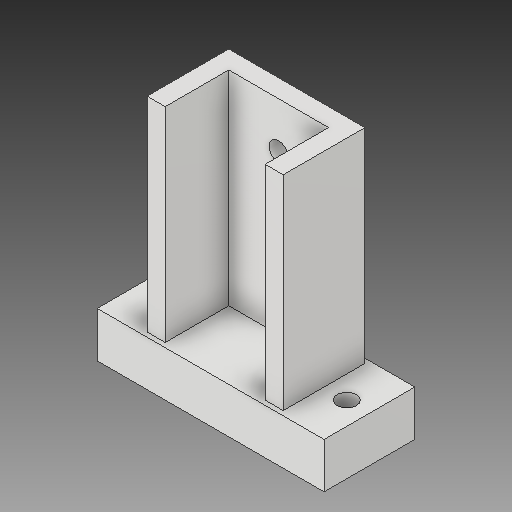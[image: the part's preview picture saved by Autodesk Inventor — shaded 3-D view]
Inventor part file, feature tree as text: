
AUTODESK INVENTOR PART (.ipt)
format: ipt  version: 2019 (Build 230136000, 136)  size: 143,872 bytes
history: native  units: mm
features: extrude x4, sketch x4, projected_geometry x1
ambient origin geometry x8: Origin, YZ Plane, XZ Plane, XY Plane, X Axis, Y Axis, Z Axis, Center Point
bodies: Body1 (feature_tree)
feature tree (9):
  extrude  "Extrusion3"  Depth=50.0mm
  extrude  "Extrusion4"  Depth=22.0mm
  extrude  "Extrusion5"  Depth=4.0mm
  extrude  "Extrusion6"  Depth=14.0mm
  sketch  "Sketch2"  dims[d10=20.0mm d11=50.0mm]
  sketch  "Sketch3"  dims[d12=10.0mm d13=0.0mm d14=22.0mm]
  projected_geometry  "Projected Loop1"
  sketch  "Sketch4"  dims[d15=4.0mm d16=4.0mm]
  sketch  "Sketch5"  dims[d17=1.0mm d18=14.0mm d19=45.0mm d20=0.0mm d21=4.25mm d22=8.0mm d23=13.0mm d24=0.0mm d26=4.25mm d27=10.0mm d28=5.0mm d29=10.0mm d30=0.0mm]
